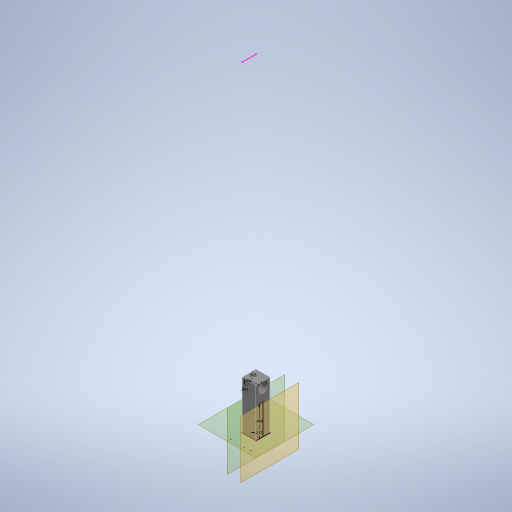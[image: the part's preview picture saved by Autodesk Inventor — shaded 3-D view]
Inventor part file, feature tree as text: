
AUTODESK INVENTOR PART (.ipt)
format: ipt  version: 2024 (Build 280153000, 153)  size: 376,320 bytes
history: native  units: in
note: dims shown in document units (in); Inventor stores cm internally (conversion verified against a paired STEP export)
features: plane x5, sketch x4, hole x2, extrude x2, thread x1
ambient origin geometry x8: Origin, YZ Plane, XZ Plane, XY Plane, X Axis, Y Axis, Z Axis, Center Point
bodies: Solid1 (feature_tree)
feature tree (14):
  plane  "Work Plane2"
  sketch  "Sketch1"  dims[d24=0.454in d25=0.0405in]
  plane  "Work Plane1"
  sketch  "Sketch2"  dims[d26=0.098in d27=0.12in]
  plane  "Work Plane3"
  plane  "Work Plane6"
  sketch  "Sketch5"  dims[d28=0.12in d29=0.75in d30=0.375in d31=0.25in d32=0.5635in d33=1.0in d34=0.8108in d35=0.112in]
  hole  "Hole3"  [1 undecoded]
  plane  "Work Plane5"
  sketch  "Sketch6"  dims[d36=0.72in d37=0.0in d38=0.12in d39=0.75in d40=0.375in d41=0.25in d42=0.5635in d43=1.0in d44=0.8108in d45=0.46in d46=0.0in d47=0.46in d48=0.0in d17=1.0in d18=1.0in d19=1.0in d20=0.15in d21=0.25in d22=0.375in d23=0.5635in]
  extrude  "Extrusion3"  Depth=0.12in
  hole  "Hole4"  [1 undecoded]
  extrude  "Extrusion4"  Depth=0.46in TaperAngle=0.0deg
  thread  "Thread1"  [1 undecoded]
note: 3 required parameter values undecoded (feature->parameter linkage not recoverable at this tier; creation-order binding heuristic only, values carry confidence <= 0.55)
